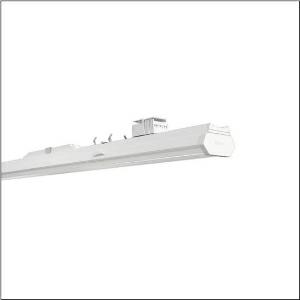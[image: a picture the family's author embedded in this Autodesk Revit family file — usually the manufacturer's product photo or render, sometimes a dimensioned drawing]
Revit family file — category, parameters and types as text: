
# Revit family: licross_21_protected_mo_52td12dn4a5g3s
name_source: partatom
category: Lighting Fixtures
units: mm (PartAtom-declared; Revit-internal decimal feet)

## family parameters
Cut with Voids When Loaded = No
Host = Face
Light Source = No
Part Type = Normal
Room Calculation Point = No
Round Connector Dimension = Use Diameter
Shared = No

## types (1)
- --- (1 x LED, 940 lm, 6.8 W, 4000K)
    Apparent Load = 7 VA
    CIE Flux Codes = 73 92 98 99 100
    Color Rendering = 80
    Color Temperature = 4000K
    Default Elevation = 1800 mm
    Description = Licross 21 Protected MO, luminaire insert, of sheet steel, galvanised, coil coated, white, length: 1.500mm, width: 90mm, height: 103mm, LED rated luminous flux: 10.700lm, light colour: 840, SDCM (Standard Deviation of Colour Matching)MacAdam ≤ 3 SDCM (initial), control gear: DALI 2 (for two DALI lines), with plug, 6-pole, with phase selection, for trunking rail, 14-core, mains connection: 220..240V, AC, 50/60Hz, rated input power: 66W, for trunking rail, 14-core, internal wiring halogen-free, for emergency light function, converter,control gear: single battery element, battery: LiFePO4, 9Ah, primary light control with lens, of plastic, primary optical cover: cover, of PMMA, light emission: direct distribution, primary light characteristic: symmetric, protection rating (complete): IP54, insulation class (complete): insulation class I (protective earthing), certification: CE, UKCA, protection symbol: D if used in an environment with non-conductive dust loads with corresponding accessories, impact resistance: IK06, permissible ambient temperature for indoor applications: +5..+35°C, standard: EN 60598-2-22, LABS conformity tested according to VDMA 24364:2018-05, reducing of maximum allowable ambient temperature of 5°C with ceiling mounting, corresponds to IFS (International Featured Standards) requirements for safety and quality in the food industry, The light source and the operating device comply with the requirements of the Ecodesign Regulation (EU) 2019/2020 and are replaceable in accordance with this regulation, packaging unit: 1 piece
    Height = 92 mm
    Lamp = 1 x LED
    Lamp Light Flux = 940 lm
    Lamp Power = 6.8 W
    Lamp count = 1
    Length = 1500 mm
    Luminous efficacy = 138 lm/W
    Manufacturer = Siteco
    ModVariant = No
    Model = 52TD12DN4A5G3S
    Mounting Place = Ceiling
    Mounting Type = Pendant
    Number of Poles = 1
    OnlyDefault = Yes
    Power Factor = 1
    Product Name = Licross 21 Protected MO
    Product group = luminaire insert | ceiling pendant
    ProductGroupID = 901
    Protection Class = Protection class I
    Protection Degree = IP 54
    RLX_Detail_Level = 1
    RLX_Emergency_Light_Flux = 0 lm
    RLX_Emergency_Type = 0
    RLX_Emergency_Type_DB = No
    RlxData = <blob elided: 25173 chars, md5=990eb9fe>
    Socket = socket
    Standby Power = 0 W
    System Light Flux = 940 lm
    System Power = 7 W
    Type Comments = : emergency light operation: 3 h
    Type Image = l_1256148.jpg
    URL = http://relux.com
    VarID = @adj_110883
    Voltage = 0 V
    Weight = 0.00 kg
    Width = 88 mm

## geometry (parser evidence)
native form markers: Blend x4, Sweep x9
no freeform markers — native parametric forms only
